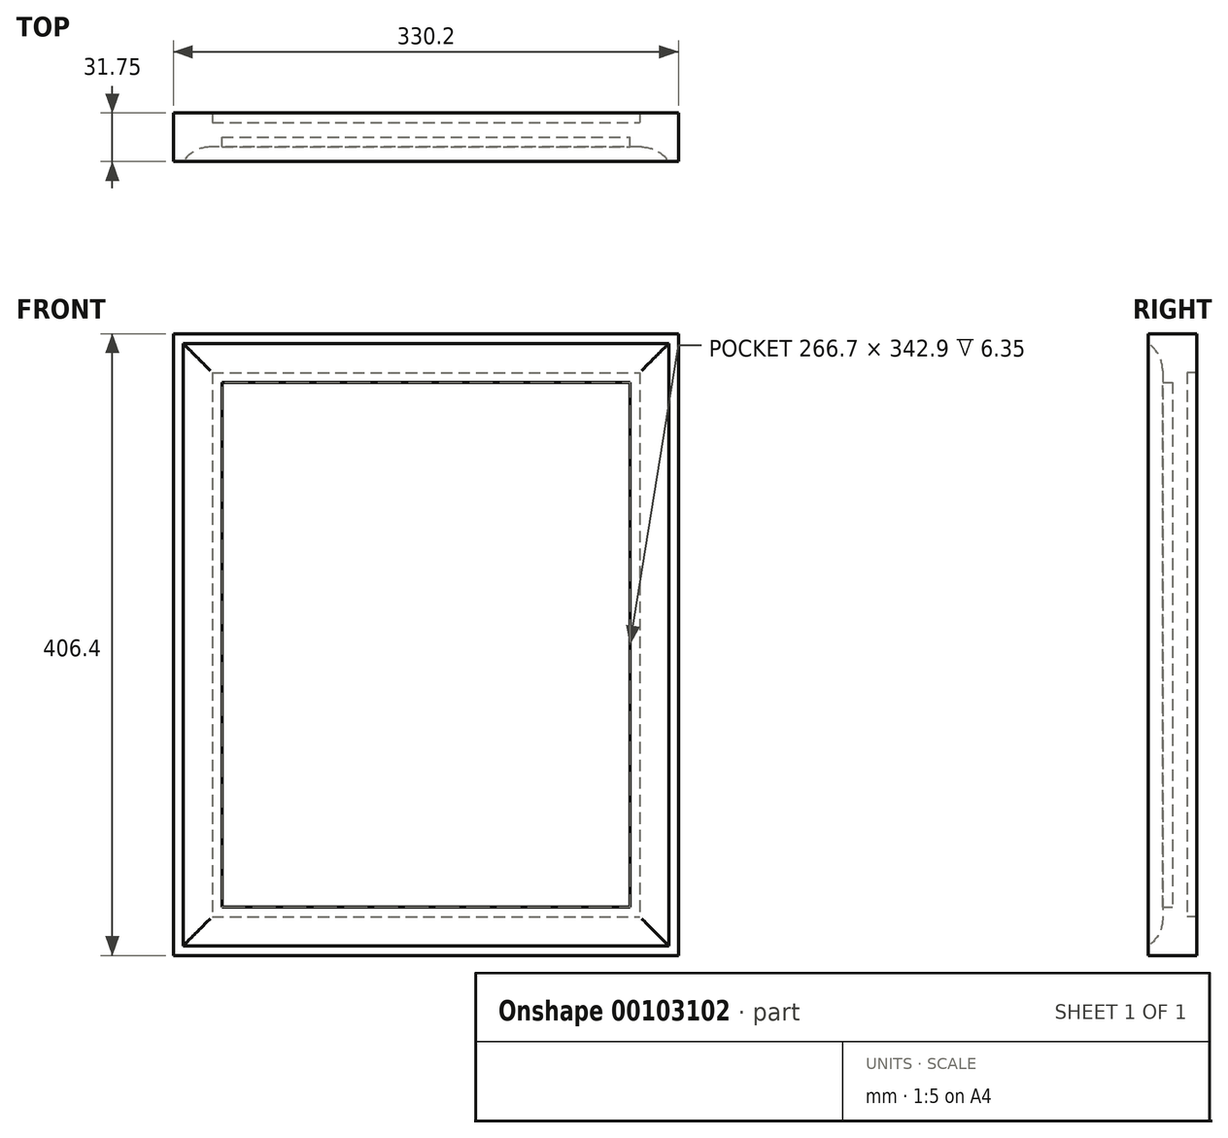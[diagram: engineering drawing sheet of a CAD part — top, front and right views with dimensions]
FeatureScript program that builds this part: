
annotation { "Feature Type Name" : "Feature", "Feature Type Description" : "" }
export const myFeature = defineFeature(function(context is Context, id is Id, definition is map)
    precondition{}
    {
        {
            var Q0;
            Q0=qCreatedBy(makeId("Front.planeOp"),FACE);
            var sketch = newSketch(context, id + "F0", { "sketchPlane" : qUnion([Q0])});
            skLineSegment(sketch, "E0.bottom", {"start": v(-139.7, 177.8) * mm, "end": v(139.7, 177.8) * mm});
            skLineSegment(sketch, "E0.top", {"start": v(-139.7, -177.8) * mm, "end": v(139.7, -177.8) * mm});
            skLineSegment(sketch, "E0.left", {"start": v(-139.7, 177.8) * mm, "end": v(-139.7, -177.8) * mm});
            skLineSegment(sketch, "E0.right", {"start": v(139.7, 177.8) * mm, "end": v(139.7, -177.8) * mm});
            skSolve(sketch);
        }
        {
            var Q0;
            Q0=makeQuery(id+"F0.imprint","IMPRINT",FACE,{"disambiguationData":[TD([[makeQuery(id+"F0.imprint","IMPRINT",EDGE,{"derivedFrom":sQuery(id+"F0.wireOp",EDGE,"E0.bottom")}),-1.0]])]});
            extrude(context, id + "F1", {"entities" : qUnion([Q0]), "depth" : 9.52 * mm});
        }
        {
            var Q0;
            Q0=makeQuery(id+"F1.opExtrude","CAP_FACE",FACE,{"disambiguationData":[OSD([sQuery(id+"F0.wireOp",EDGE,"E0.bottom"),sQuery(id+"F0.wireOp",EDGE,"E0.top"),sQuery(id+"F0.wireOp",EDGE,"E0.left"),sQuery(id+"F0.wireOp",EDGE,"E0.right")])],"isStart":false});
            var sketch = newSketch(context, id + "F2", { "sketchPlane" : qUnion([Q0])});
            skLineSegment(sketch, "E1.bottom", {"start": v(-165.1, 203.2) * mm, "end": v(165.1, 203.2) * mm});
            skLineSegment(sketch, "E1.top", {"start": v(-165.1, -203.2) * mm, "end": v(165.1, -203.2) * mm});
            skLineSegment(sketch, "E1.left", {"start": v(-165.1, 203.2) * mm, "end": v(-165.1, -203.2) * mm});
            skLineSegment(sketch, "E1.right", {"start": v(165.1, 203.2) * mm, "end": v(165.1, -203.2) * mm});
            skLineSegment(sketch, "E2.bottom", {"start": v(-133.35, 171.45) * mm, "end": v(133.35, 171.45) * mm});
            skLineSegment(sketch, "E2.top", {"start": v(-133.35, -171.45) * mm, "end": v(133.35, -171.45) * mm});
            skLineSegment(sketch, "E2.left", {"start": v(-133.35, 171.45) * mm, "end": v(-133.35, -171.45) * mm});
            skLineSegment(sketch, "E2.right", {"start": v(133.35, 171.45) * mm, "end": v(133.35, -171.45) * mm});
            skSolve(sketch);
        }
        {
            var Q0;
            Q0=makeQuery(id+"F2.imprint","IMPRINT",FACE,{"disambiguationData":[TD([[makeQuery(id+"F2.imprint","IMPRINT",EDGE,{"derivedFrom":sQuery(id+"F2.wireOp",EDGE,"E1.bottom")}),-1.0]])]});
            var Q1;
            Q1=makeQuery(id+"F2.imprint","IMPRINT",FACE,{"disambiguationData":[TD([[makeQuery(id+"F2.imprint","IMPRINT",EDGE,{"derivedFrom":sQuery(id+"F2.wireOp",EDGE,"E2.bottom")}),1.0]])]});
            extrude(context, id + "F3", {"entities" : qUnion([Q0, Q1]), "depth" : 15.88 * mm});
        }
        {
            var Q0;
            Q0=makeQuery(id+"F3.opExtrude","CAP_FACE",FACE,{"disambiguationData":[OSD([sQuery(id+"F0.wireOp",EDGE,"E0.bottom"),sQuery(id+"F0.wireOp",EDGE,"E0.top"),sQuery(id+"F0.wireOp",EDGE,"E0.left"),sQuery(id+"F0.wireOp",EDGE,"E0.right"),sQuery(id+"F2.wireOp",EDGE,"E1.bottom"),sQuery(id+"F2.wireOp",EDGE,"E1.top"),sQuery(id+"F2.wireOp",EDGE,"E1.left"),sQuery(id+"F2.wireOp",EDGE,"E1.right")])],"isStart":true});
            var sketch = newSketch(context, id + "F4", { "sketchPlane" : qUnion([Q0])});
            skLineSegment(sketch, "E3.bottom", {"start": v(-139.7, 177.8) * mm, "end": v(139.7, 177.8) * mm});
            skLineSegment(sketch, "E3.top", {"start": v(-139.7, -177.8) * mm, "end": v(139.7, -177.8) * mm});
            skLineSegment(sketch, "E3.left", {"start": v(-139.7, 177.8) * mm, "end": v(-139.7, -177.8) * mm});
            skLineSegment(sketch, "E3.right", {"start": v(139.7, 177.8) * mm, "end": v(139.7, -177.8) * mm});
            skLineSegment(sketch, "E4.bottom", {"start": v(-165.1, 203.2) * mm, "end": v(165.1, 203.2) * mm});
            skLineSegment(sketch, "E4.top", {"start": v(-165.1, -203.2) * mm, "end": v(165.1, -203.2) * mm});
            skLineSegment(sketch, "E4.left", {"start": v(-165.1, 203.2) * mm, "end": v(-165.1, -203.2) * mm});
            skLineSegment(sketch, "E4.right", {"start": v(165.1, 203.2) * mm, "end": v(165.1, -203.2) * mm});
            skSolve(sketch);
        }
        {
            var Q0;
            Q0=makeQuery(id+"F4.imprint","IMPRINT",FACE,{"disambiguationData":[TD([[makeQuery(id+"F4.imprint","IMPRINT",EDGE,{"derivedFrom":sQuery(id+"F4.wireOp",EDGE,"E3.bottom")}),1.0]])]});
            extrude(context, id + "F5", {"entities" : qUnion([Q0]), "operationType" : NewBodyOperationType.ADD, "depth" : 15.88 * mm});
        }
        {
            var Q0;
            Q0=qCreatedBy(makeId("Top.planeOp"),FACE);
            var sketch = newSketch(context, id + "F6", { "sketchPlane" : qUnion([Q0])});
            skLineSegment(sketch, "E5", {"start": v(-133.35, -25.4) * mm, "end": v(-158.75, -25.4) * mm});
            skLineSegment(sketch, "E6", {"start": v(-133.35, -25.4) * mm, "end": v(-133.35, -15.87) * mm});
            skLineSegment(sketch, "E7", {"start": v(-133.35, -15.87) * mm, "end": v(-140.97, -15.87) * mm});
            skArc(sketch, "E8", {"start": v(-140.97, -15.87) * mm, "mid": v(-151.06, -18.4) * mm, "end": v(-158.75, -25.4) * mm});
            skSolve(sketch);
        }
        {
            var Q0;
            Q0=makeQuery(id+"F6.imprint","IMPRINT",FACE,{"disambiguationData":[TD([[makeQuery(id+"F6.imprint","IMPRINT",EDGE,{"derivedFrom":sQuery(id+"F6.wireOp",EDGE,"E5")}),-1.0]])]});
            var Q1;
            Q1=makeQuery(id+"F3.opExtrude","CAP_EDGE",EDGE,{"disambiguationData":[OSD([sQuery(id+"F2.wireOp",EDGE,"E2.left")])],"isStart":false});
            var Q2;
            Q2=makeQuery(id+"F3.opExtrude","CAP_EDGE",EDGE,{"disambiguationData":[OSD([sQuery(id+"F2.wireOp",EDGE,"E2.bottom")])],"isStart":false});
            var Q3;
            Q3=makeQuery(id+"F3.opExtrude","CAP_EDGE",EDGE,{"disambiguationData":[OSD([sQuery(id+"F2.wireOp",EDGE,"E2.right")])],"isStart":false});
            var Q4;
            Q4=makeQuery(id+"F3.opExtrude","CAP_EDGE",EDGE,{"disambiguationData":[OSD([sQuery(id+"F2.wireOp",EDGE,"E2.top")])],"isStart":false});
            sweep(context, id + "F7", {"operationType" : NewBodyOperationType.REMOVE, "profiles" : qUnion([Q0]), "path" : qUnion([Q1, Q2, Q3, Q4])});
        }
    });
